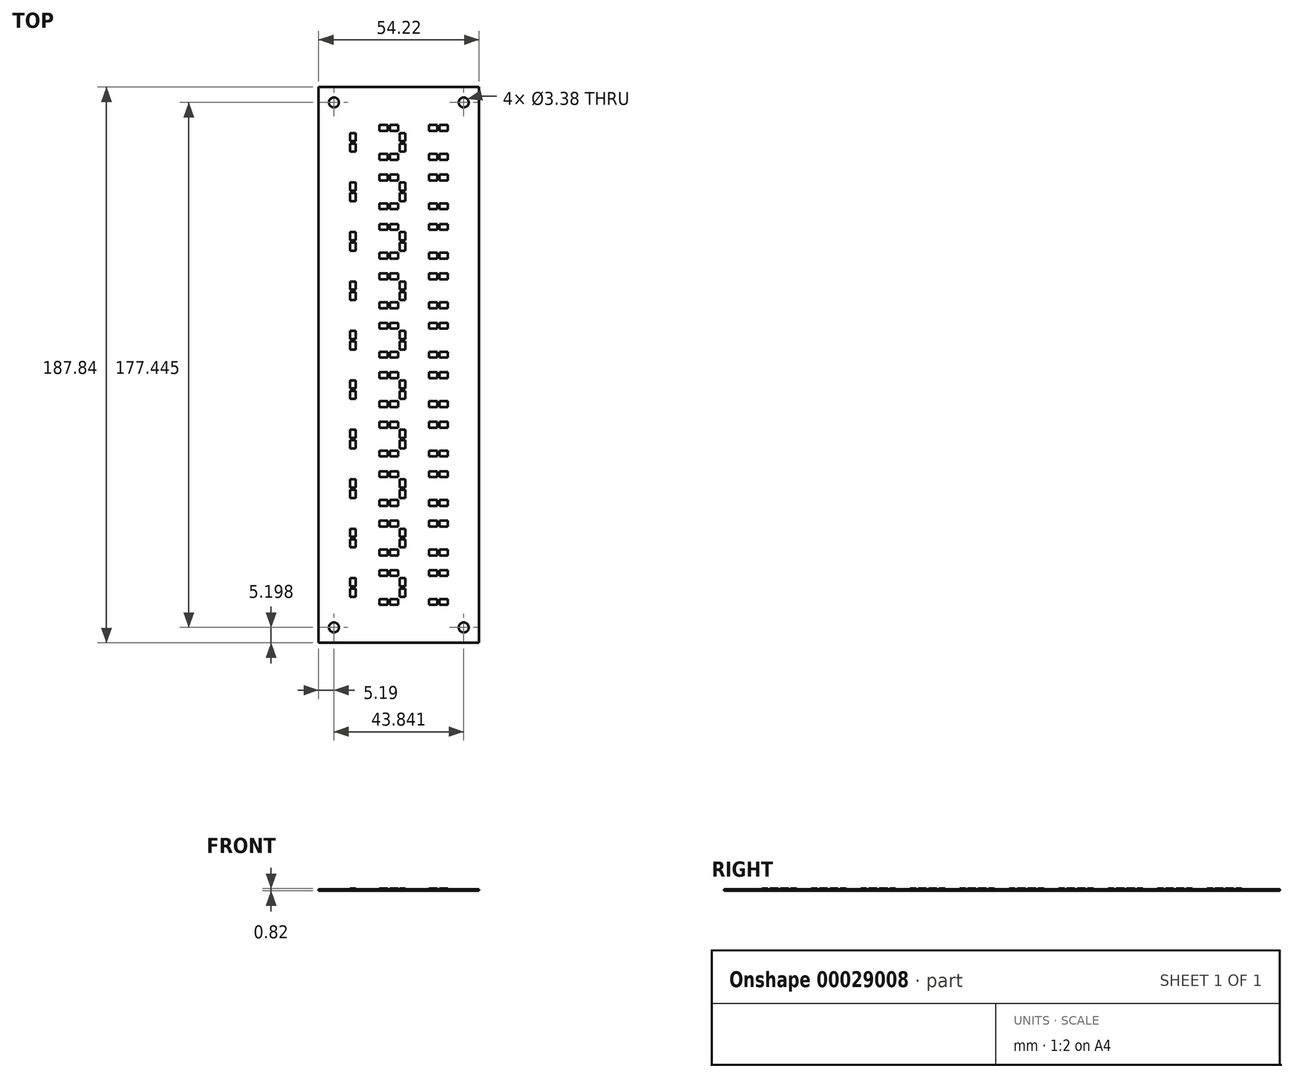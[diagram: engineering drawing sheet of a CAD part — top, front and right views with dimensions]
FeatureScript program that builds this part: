
annotation { "Feature Type Name" : "Feature", "Feature Type Description" : "" }
export const myFeature = defineFeature(function(context is Context, id is Id, definition is map)
    precondition{}
    {
        {
            var Q0;
            Q0=qCreatedBy(makeId("Top.planeOp"),FACE);
            var sketch = newSketch(context, id + "F0", { "sketchPlane" : qUnion([Q0])});
            skLineSegment(sketch, "E0.rect.bottom", {"start": v(-27.11, 93.92) * mm, "end": v(27.11, 93.92) * mm});
            skLineSegment(sketch, "E0.rect.top", {"start": v(-27.11, -93.92) * mm, "end": v(27.11, -93.92) * mm});
            skLineSegment(sketch, "E0.rect.left", {"start": v(-27.11, 93.92) * mm, "end": v(-27.11, -93.92) * mm});
            skLineSegment(sketch, "E0.rect.right", {"start": v(27.11, 93.92) * mm, "end": v(27.11, -93.92) * mm});
            skPoint(sketch, "E0.rect.middle", {"position": v(0, 0) * mm});
            skCircle(sketch, "E1", {"center": v(-21.92, 88.72) * mm, "radius": 1.69 * mm});
            skCircle(sketch, "E2", {"center": v(21.92, 88.72) * mm, "radius": 1.69 * mm});
            skCircle(sketch, "E3", {"center": v(21.92, -88.72) * mm, "radius": 1.69 * mm});
            skCircle(sketch, "E4", {"center": v(-21.92, -88.72) * mm, "radius": 1.69 * mm});
            skSolve(sketch);
        }
        {
            var Q0;
            Q0 = qSketchRegion(id + "F0", true);
            extrude(context, id + "F1", {"entities" : qUnion([Q0]), "depth" : .57 * mm});
        }
        {
            var Q0;
            Q0=makeQuery(id+"F1.opExtrude","CAP_FACE",FACE,{"disambiguationData":[OSD([sQuery(id+"F0.wireOp",EDGE,"E0.rect.bottom"),sQuery(id+"F0.wireOp",EDGE,"E0.rect.top"),sQuery(id+"F0.wireOp",EDGE,"E0.rect.left"),sQuery(id+"F0.wireOp",EDGE,"E0.rect.right"),sQuery(id+"F0.wireOp",EDGE,"E1"),sQuery(id+"F0.wireOp",EDGE,"E2"),sQuery(id+"F0.wireOp",EDGE,"E3"),sQuery(id+"F0.wireOp",EDGE,"E4")])],"isStart":false});
            var sketch = newSketch(context, id + "F2", { "sketchPlane" : qUnion([Q0])});
            skLineSegment(sketch, "E5.bottom", {"start": v(-16.54, -78.36) * mm, "end": v(-14.55, -78.36) * mm});
            skLineSegment(sketch, "E5.top", {"start": v(-16.54, -75.62) * mm, "end": v(-14.55, -75.62) * mm});
            skLineSegment(sketch, "E5.left", {"start": v(-16.54, -78.36) * mm, "end": v(-16.54, -75.62) * mm});
            skLineSegment(sketch, "E5.right", {"start": v(-14.55, -78.36) * mm, "end": v(-14.55, -75.62) * mm});
            skLineSegment(sketch, "E6.bottom", {"start": v(-6.53, -79.1) * mm, "end": v(-3.8, -79.1) * mm});
            skLineSegment(sketch, "E6.top", {"start": v(-6.53, -81.08) * mm, "end": v(-3.8, -81.08) * mm});
            skLineSegment(sketch, "E6.left", {"start": v(-6.53, -79.1) * mm, "end": v(-6.53, -81.08) * mm});
            skLineSegment(sketch, "E6.right", {"start": v(-3.8, -79.1) * mm, "end": v(-3.8, -81.08) * mm});
            skLineSegment(sketch, "E7.bottom", {"start": v(-16.54, -74.8) * mm, "end": v(-14.55, -74.8) * mm});
            skLineSegment(sketch, "E7.top", {"start": v(-16.54, -72.06) * mm, "end": v(-14.55, -72.06) * mm});
            skLineSegment(sketch, "E7.left", {"start": v(-16.54, -74.8) * mm, "end": v(-16.54, -72.06) * mm});
            skLineSegment(sketch, "E7.right", {"start": v(-14.55, -74.8) * mm, "end": v(-14.55, -72.06) * mm});
            skLineSegment(sketch, "E8.left", {"start": v(-2.98, -79.1) * mm, "end": v(-2.98, -81.08) * mm});
            skLineSegment(sketch, "E8.top", {"start": v(-2.98, -81.08) * mm, "end": v(-0.24, -81.08) * mm});
            skLineSegment(sketch, "E8.right", {"start": v(-0.24, -79.1) * mm, "end": v(-0.24, -81.08) * mm});
            skLineSegment(sketch, "E8.bottom", {"start": v(-2.98, -79.1) * mm, "end": v(-0.24, -79.1) * mm});
            skLineSegment(sketch, "E9.top", {"start": v(-2.98, -71.32) * mm, "end": v(-0.24, -71.32) * mm});
            skLineSegment(sketch, "E10.right", {"start": v(-3.8, -69.34) * mm, "end": v(-3.8, -71.32) * mm});
            skLineSegment(sketch, "E9.left", {"start": v(-2.98, -69.34) * mm, "end": v(-2.98, -71.32) * mm});
            skLineSegment(sketch, "E10.top", {"start": v(-6.53, -71.32) * mm, "end": v(-3.8, -71.32) * mm});
            skLineSegment(sketch, "E10.bottom", {"start": v(-6.53, -69.34) * mm, "end": v(-3.8, -69.34) * mm});
            skLineSegment(sketch, "E9.bottom", {"start": v(-2.98, -69.34) * mm, "end": v(-0.24, -69.34) * mm});
            skLineSegment(sketch, "E9.right", {"start": v(-0.24, -69.34) * mm, "end": v(-0.24, -71.32) * mm});
            skLineSegment(sketch, "E10.left", {"start": v(-6.53, -69.34) * mm, "end": v(-6.53, -71.32) * mm});
            skLineSegment(sketch, "E11.top", {"start": v(13.79, -71.32) * mm, "end": v(16.53, -71.32) * mm});
            skLineSegment(sketch, "E12.top", {"start": v(13.79, -81.08) * mm, "end": v(16.53, -81.08) * mm});
            skLineSegment(sketch, "E11.right", {"start": v(16.53, -69.34) * mm, "end": v(16.53, -71.32) * mm});
            skLineSegment(sketch, "E11.bottom", {"start": v(13.79, -69.34) * mm, "end": v(16.53, -69.34) * mm});
            skLineSegment(sketch, "E13.right", {"start": v(2.21, -78.36) * mm, "end": v(2.21, -75.62) * mm});
            skLineSegment(sketch, "E13.left", {"start": v(0.23, -78.36) * mm, "end": v(0.23, -75.62) * mm});
            skLineSegment(sketch, "E13.top", {"start": v(0.23, -75.62) * mm, "end": v(2.21, -75.62) * mm});
            skLineSegment(sketch, "E13.bottom", {"start": v(0.23, -78.36) * mm, "end": v(2.21, -78.36) * mm});
            skLineSegment(sketch, "E12.bottom", {"start": v(13.79, -79.1) * mm, "end": v(16.53, -79.1) * mm});
            skLineSegment(sketch, "E12.right", {"start": v(16.53, -79.1) * mm, "end": v(16.53, -81.08) * mm});
            skLineSegment(sketch, "E14.top", {"start": v(0.23, -72.06) * mm, "end": v(2.21, -72.06) * mm});
            skLineSegment(sketch, "E14.bottom", {"start": v(0.23, -74.8) * mm, "end": v(2.21, -74.8) * mm});
            skLineSegment(sketch, "E11.left", {"start": v(13.79, -69.34) * mm, "end": v(13.79, -71.32) * mm});
            skLineSegment(sketch, "E15.bottom", {"start": v(10.23, -69.34) * mm, "end": v(12.98, -69.34) * mm});
            skLineSegment(sketch, "E15.right", {"start": v(12.98, -69.34) * mm, "end": v(12.98, -71.32) * mm});
            skLineSegment(sketch, "E15.top", {"start": v(10.23, -71.32) * mm, "end": v(12.98, -71.32) * mm});
            skLineSegment(sketch, "E15.left", {"start": v(10.23, -69.34) * mm, "end": v(10.23, -71.32) * mm});
            skLineSegment(sketch, "E12.left", {"start": v(13.79, -79.1) * mm, "end": v(13.79, -81.08) * mm});
            skLineSegment(sketch, "E14.right", {"start": v(2.21, -74.8) * mm, "end": v(2.21, -72.06) * mm});
            skLineSegment(sketch, "E16.left", {"start": v(10.23, -79.1) * mm, "end": v(10.23, -81.08) * mm});
            skLineSegment(sketch, "E16.top", {"start": v(10.23, -81.08) * mm, "end": v(12.98, -81.08) * mm});
            skLineSegment(sketch, "E16.bottom", {"start": v(10.23, -79.1) * mm, "end": v(12.98, -79.1) * mm});
            skLineSegment(sketch, "E14.left", {"start": v(0.23, -74.8) * mm, "end": v(0.23, -72.06) * mm});
            skLineSegment(sketch, "E16.right", {"start": v(12.98, -79.1) * mm, "end": v(12.98, -81.08) * mm});
            skLineSegment(sketch, "E17.left", {"start": v(0.23, -61.65) * mm, "end": v(0.23, -58.9) * mm});
            skLineSegment(sketch, "E18.bottom", {"start": v(-16.54, -61.65) * mm, "end": v(-14.55, -61.65) * mm});
            skLineSegment(sketch, "E19.right", {"start": v(-0.24, -62.38) * mm, "end": v(-0.24, -64.36) * mm});
            skLineSegment(sketch, "E18.top", {"start": v(-16.54, -58.9) * mm, "end": v(-14.55, -58.9) * mm});
            skLineSegment(sketch, "E20.top", {"start": v(-2.98, -54.61) * mm, "end": v(-0.24, -54.61) * mm});
            skLineSegment(sketch, "E19.top", {"start": v(-2.98, -64.36) * mm, "end": v(-0.24, -64.36) * mm});
            skLineSegment(sketch, "E17.right", {"start": v(2.21, -61.65) * mm, "end": v(2.21, -58.9) * mm});
            skLineSegment(sketch, "E21.top", {"start": v(13.79, -54.61) * mm, "end": v(16.53, -54.61) * mm});
            skLineSegment(sketch, "E17.top", {"start": v(0.23, -58.9) * mm, "end": v(2.21, -58.9) * mm});
            skLineSegment(sketch, "E22.right", {"start": v(16.53, -62.38) * mm, "end": v(16.53, -64.36) * mm});
            skLineSegment(sketch, "E18.left", {"start": v(-16.54, -61.65) * mm, "end": v(-16.54, -58.9) * mm});
            skLineSegment(sketch, "E18.right", {"start": v(-14.55, -61.65) * mm, "end": v(-14.55, -58.9) * mm});
            skLineSegment(sketch, "E23.bottom", {"start": v(-16.54, -58.09) * mm, "end": v(-14.55, -58.09) * mm});
            skLineSegment(sketch, "E23.top", {"start": v(-16.54, -55.35) * mm, "end": v(-14.55, -55.35) * mm});
            skLineSegment(sketch, "E22.top", {"start": v(13.79, -64.36) * mm, "end": v(16.53, -64.36) * mm});
            skLineSegment(sketch, "E17.bottom", {"start": v(0.23, -61.65) * mm, "end": v(2.21, -61.65) * mm});
            skLineSegment(sketch, "E24.top", {"start": v(0.23, -55.35) * mm, "end": v(2.21, -55.35) * mm});
            skLineSegment(sketch, "E21.right", {"start": v(16.53, -52.63) * mm, "end": v(16.53, -54.61) * mm});
            skLineSegment(sketch, "E24.bottom", {"start": v(0.23, -58.09) * mm, "end": v(2.21, -58.09) * mm});
            skLineSegment(sketch, "E25.top", {"start": v(10.23, -54.61) * mm, "end": v(12.98, -54.61) * mm});
            skLineSegment(sketch, "E21.bottom", {"start": v(13.79, -52.63) * mm, "end": v(16.53, -52.63) * mm});
            skLineSegment(sketch, "E26.left", {"start": v(10.23, -62.38) * mm, "end": v(10.23, -64.36) * mm});
            skLineSegment(sketch, "E21.left", {"start": v(13.79, -52.63) * mm, "end": v(13.79, -54.61) * mm});
            skLineSegment(sketch, "E27.right", {"start": v(-3.8, -52.63) * mm, "end": v(-3.8, -54.61) * mm});
            skLineSegment(sketch, "E19.bottom", {"start": v(-2.98, -62.38) * mm, "end": v(-0.24, -62.38) * mm});
            skLineSegment(sketch, "E27.left", {"start": v(-6.53, -52.63) * mm, "end": v(-6.53, -54.61) * mm});
            skLineSegment(sketch, "E27.bottom", {"start": v(-6.53, -52.63) * mm, "end": v(-3.8, -52.63) * mm});
            skLineSegment(sketch, "E26.bottom", {"start": v(10.23, -62.38) * mm, "end": v(12.98, -62.38) * mm});
            skLineSegment(sketch, "E22.bottom", {"start": v(13.79, -62.38) * mm, "end": v(16.53, -62.38) * mm});
            skLineSegment(sketch, "E26.top", {"start": v(10.23, -64.36) * mm, "end": v(12.98, -64.36) * mm});
            skLineSegment(sketch, "E25.left", {"start": v(10.23, -52.63) * mm, "end": v(10.23, -54.61) * mm});
            skLineSegment(sketch, "E25.bottom", {"start": v(10.23, -52.63) * mm, "end": v(12.98, -52.63) * mm});
            skLineSegment(sketch, "E20.bottom", {"start": v(-2.98, -52.63) * mm, "end": v(-0.24, -52.63) * mm});
            skLineSegment(sketch, "E24.left", {"start": v(0.23, -58.09) * mm, "end": v(0.23, -55.35) * mm});
            skLineSegment(sketch, "E28.bottom", {"start": v(-6.53, -62.38) * mm, "end": v(-3.8, -62.38) * mm});
            skLineSegment(sketch, "E28.top", {"start": v(-6.53, -64.36) * mm, "end": v(-3.8, -64.36) * mm});
            skLineSegment(sketch, "E28.left", {"start": v(-6.53, -62.38) * mm, "end": v(-6.53, -64.36) * mm});
            skLineSegment(sketch, "E28.right", {"start": v(-3.8, -62.38) * mm, "end": v(-3.8, -64.36) * mm});
            skLineSegment(sketch, "E23.left", {"start": v(-16.54, -58.09) * mm, "end": v(-16.54, -55.35) * mm});
            skLineSegment(sketch, "E23.right", {"start": v(-14.55, -58.09) * mm, "end": v(-14.55, -55.35) * mm});
            skLineSegment(sketch, "E22.left", {"start": v(13.79, -62.38) * mm, "end": v(13.79, -64.36) * mm});
            skLineSegment(sketch, "E19.left", {"start": v(-2.98, -62.38) * mm, "end": v(-2.98, -64.36) * mm});
            skLineSegment(sketch, "E25.right", {"start": v(12.98, -52.63) * mm, "end": v(12.98, -54.61) * mm});
            skLineSegment(sketch, "E20.right", {"start": v(-0.24, -52.63) * mm, "end": v(-0.24, -54.61) * mm});
            skLineSegment(sketch, "E26.right", {"start": v(12.98, -62.38) * mm, "end": v(12.98, -64.36) * mm});
            skLineSegment(sketch, "E20.left", {"start": v(-2.98, -52.63) * mm, "end": v(-2.98, -54.61) * mm});
            skLineSegment(sketch, "E24.right", {"start": v(2.21, -58.09) * mm, "end": v(2.21, -55.35) * mm});
            skLineSegment(sketch, "E27.top", {"start": v(-6.53, -54.61) * mm, "end": v(-3.8, -54.61) * mm});
            skLineSegment(sketch, "E29.top", {"start": v(0.23, -25.48) * mm, "end": v(2.21, -25.48) * mm});
            skLineSegment(sketch, "E30.top", {"start": v(13.79, -37.9) * mm, "end": v(16.53, -37.9) * mm});
            skLineSegment(sketch, "E31.top", {"start": v(0.23, -38.63) * mm, "end": v(2.21, -38.63) * mm});
            skLineSegment(sketch, "E32.top", {"start": v(13.79, -47.65) * mm, "end": v(16.53, -47.65) * mm});
            skLineSegment(sketch, "E33.top", {"start": v(-2.98, -47.65) * mm, "end": v(-0.24, -47.65) * mm});
            skLineSegment(sketch, "E34.bottom", {"start": v(0.23, -24.66) * mm, "end": v(2.21, -24.66) * mm});
            skLineSegment(sketch, "E35.left", {"start": v(-16.54, -28.22) * mm, "end": v(-16.54, -25.48) * mm});
            skLineSegment(sketch, "E30.right", {"start": v(16.53, -35.92) * mm, "end": v(16.53, -37.9) * mm});
            skLineSegment(sketch, "E31.bottom", {"start": v(0.23, -41.38) * mm, "end": v(2.21, -41.38) * mm});
            skLineSegment(sketch, "E36.left", {"start": v(-16.54, -44.93) * mm, "end": v(-16.54, -42.19) * mm});
            skLineSegment(sketch, "E36.right", {"start": v(-14.55, -44.93) * mm, "end": v(-14.55, -42.19) * mm});
            skLineSegment(sketch, "E37.top", {"start": v(-2.98, -37.9) * mm, "end": v(-0.24, -37.9) * mm});
            skLineSegment(sketch, "E38.top", {"start": v(13.79, -21.18) * mm, "end": v(16.53, -21.18) * mm});
            skLineSegment(sketch, "E29.left", {"start": v(0.23, -28.22) * mm, "end": v(0.23, -25.48) * mm});
            skLineSegment(sketch, "E34.top", {"start": v(0.23, -21.92) * mm, "end": v(2.21, -21.92) * mm});
            skLineSegment(sketch, "E29.right", {"start": v(2.21, -28.22) * mm, "end": v(2.21, -25.48) * mm});
            skLineSegment(sketch, "E29.bottom", {"start": v(0.23, -28.22) * mm, "end": v(2.21, -28.22) * mm});
            skLineSegment(sketch, "E39.bottom", {"start": v(0.23, -44.93) * mm, "end": v(2.21, -44.93) * mm});
            skLineSegment(sketch, "E40.top", {"start": v(-2.98, -30.94) * mm, "end": v(-0.24, -30.94) * mm});
            skLineSegment(sketch, "E41.top", {"start": v(13.79, -30.94) * mm, "end": v(16.53, -30.94) * mm});
            skLineSegment(sketch, "E39.top", {"start": v(0.23, -42.19) * mm, "end": v(2.21, -42.19) * mm});
            skLineSegment(sketch, "E39.right", {"start": v(2.21, -44.93) * mm, "end": v(2.21, -42.19) * mm});
            skLineSegment(sketch, "E42.top", {"start": v(-2.98, -21.18) * mm, "end": v(-0.24, -21.18) * mm});
            skLineSegment(sketch, "E39.left", {"start": v(0.23, -44.93) * mm, "end": v(0.23, -42.19) * mm});
            skLineSegment(sketch, "E35.right", {"start": v(-14.55, -28.22) * mm, "end": v(-14.55, -25.48) * mm});
            skLineSegment(sketch, "E43.left", {"start": v(10.23, -35.92) * mm, "end": v(10.23, -37.9) * mm});
            skLineSegment(sketch, "E44.top", {"start": v(-6.53, -47.65) * mm, "end": v(-3.8, -47.65) * mm});
            skLineSegment(sketch, "E33.bottom", {"start": v(-2.98, -45.67) * mm, "end": v(-0.24, -45.67) * mm});
            skLineSegment(sketch, "E37.left", {"start": v(-2.98, -35.92) * mm, "end": v(-2.98, -37.9) * mm});
            skLineSegment(sketch, "E45.right", {"start": v(-14.55, -41.38) * mm, "end": v(-14.55, -38.63) * mm});
            skLineSegment(sketch, "E46.right", {"start": v(-3.8, -35.92) * mm, "end": v(-3.8, -37.9) * mm});
            skLineSegment(sketch, "E34.left", {"start": v(0.23, -24.66) * mm, "end": v(0.23, -21.92) * mm});
            skLineSegment(sketch, "E45.left", {"start": v(-16.54, -41.38) * mm, "end": v(-16.54, -38.63) * mm});
            skLineSegment(sketch, "E47.bottom", {"start": v(-6.53, -28.96) * mm, "end": v(-3.8, -28.96) * mm});
            skLineSegment(sketch, "E48.bottom", {"start": v(-6.53, -19.2) * mm, "end": v(-3.8, -19.2) * mm});
            skLineSegment(sketch, "E31.right", {"start": v(2.21, -41.38) * mm, "end": v(2.21, -38.63) * mm});
            skLineSegment(sketch, "E46.top", {"start": v(-6.53, -37.9) * mm, "end": v(-3.8, -37.9) * mm});
            skLineSegment(sketch, "E49.top", {"start": v(10.23, -21.18) * mm, "end": v(12.98, -21.18) * mm});
            skLineSegment(sketch, "E47.top", {"start": v(-6.53, -30.94) * mm, "end": v(-3.8, -30.94) * mm});
            skLineSegment(sketch, "E44.bottom", {"start": v(-6.53, -45.67) * mm, "end": v(-3.8, -45.67) * mm});
            skLineSegment(sketch, "E40.bottom", {"start": v(-2.98, -28.96) * mm, "end": v(-0.24, -28.96) * mm});
            skLineSegment(sketch, "E50.right", {"start": v(-14.55, -24.66) * mm, "end": v(-14.55, -21.92) * mm});
            skLineSegment(sketch, "E32.bottom", {"start": v(13.79, -45.67) * mm, "end": v(16.53, -45.67) * mm});
            skLineSegment(sketch, "E46.left", {"start": v(-6.53, -35.92) * mm, "end": v(-6.53, -37.9) * mm});
            skLineSegment(sketch, "E43.top", {"start": v(10.23, -37.9) * mm, "end": v(12.98, -37.9) * mm});
            skLineSegment(sketch, "E42.bottom", {"start": v(-2.98, -19.2) * mm, "end": v(-0.24, -19.2) * mm});
            skLineSegment(sketch, "E49.bottom", {"start": v(10.23, -19.2) * mm, "end": v(12.98, -19.2) * mm});
            skLineSegment(sketch, "E50.left", {"start": v(-16.54, -24.66) * mm, "end": v(-16.54, -21.92) * mm});
            skLineSegment(sketch, "E48.top", {"start": v(-6.53, -21.18) * mm, "end": v(-3.8, -21.18) * mm});
            skLineSegment(sketch, "E37.right", {"start": v(-0.24, -35.92) * mm, "end": v(-0.24, -37.9) * mm});
            skLineSegment(sketch, "E43.right", {"start": v(12.98, -35.92) * mm, "end": v(12.98, -37.9) * mm});
            skLineSegment(sketch, "E31.left", {"start": v(0.23, -41.38) * mm, "end": v(0.23, -38.63) * mm});
            skLineSegment(sketch, "E34.right", {"start": v(2.21, -24.66) * mm, "end": v(2.21, -21.92) * mm});
            skLineSegment(sketch, "E37.bottom", {"start": v(-2.98, -35.92) * mm, "end": v(-0.24, -35.92) * mm});
            skLineSegment(sketch, "E43.bottom", {"start": v(10.23, -35.92) * mm, "end": v(12.98, -35.92) * mm});
            skLineSegment(sketch, "E51.top", {"start": v(10.23, -47.65) * mm, "end": v(12.98, -47.65) * mm});
            skLineSegment(sketch, "E41.bottom", {"start": v(13.79, -28.96) * mm, "end": v(16.53, -28.96) * mm});
            skLineSegment(sketch, "E51.bottom", {"start": v(10.23, -45.67) * mm, "end": v(12.98, -45.67) * mm});
            skLineSegment(sketch, "E38.bottom", {"start": v(13.79, -19.2) * mm, "end": v(16.53, -19.2) * mm});
            skLineSegment(sketch, "E52.top", {"start": v(10.23, -30.94) * mm, "end": v(12.98, -30.94) * mm});
            skLineSegment(sketch, "E46.bottom", {"start": v(-6.53, -35.92) * mm, "end": v(-3.8, -35.92) * mm});
            skLineSegment(sketch, "E30.left", {"start": v(13.79, -35.92) * mm, "end": v(13.79, -37.9) * mm});
            skLineSegment(sketch, "E30.bottom", {"start": v(13.79, -35.92) * mm, "end": v(16.53, -35.92) * mm});
            skLineSegment(sketch, "E52.bottom", {"start": v(10.23, -28.96) * mm, "end": v(12.98, -28.96) * mm});
            skLineSegment(sketch, "E33.left", {"start": v(-2.98, -45.67) * mm, "end": v(-2.98, -47.65) * mm});
            skLineSegment(sketch, "E41.left", {"start": v(13.79, -28.96) * mm, "end": v(13.79, -30.94) * mm});
            skLineSegment(sketch, "E32.left", {"start": v(13.79, -45.67) * mm, "end": v(13.79, -47.65) * mm});
            skLineSegment(sketch, "E44.left", {"start": v(-6.53, -45.67) * mm, "end": v(-6.53, -47.65) * mm});
            skLineSegment(sketch, "E36.top", {"start": v(-16.54, -42.19) * mm, "end": v(-14.55, -42.19) * mm});
            skLineSegment(sketch, "E45.bottom", {"start": v(-16.54, -41.38) * mm, "end": v(-14.55, -41.38) * mm});
            skLineSegment(sketch, "E32.right", {"start": v(16.53, -45.67) * mm, "end": v(16.53, -47.65) * mm});
            skLineSegment(sketch, "E36.bottom", {"start": v(-16.54, -44.93) * mm, "end": v(-14.55, -44.93) * mm});
            skLineSegment(sketch, "E40.left", {"start": v(-2.98, -28.96) * mm, "end": v(-2.98, -30.94) * mm});
            skLineSegment(sketch, "E35.bottom", {"start": v(-16.54, -28.22) * mm, "end": v(-14.55, -28.22) * mm});
            skLineSegment(sketch, "E44.right", {"start": v(-3.8, -45.67) * mm, "end": v(-3.8, -47.65) * mm});
            skLineSegment(sketch, "E48.left", {"start": v(-6.53, -19.2) * mm, "end": v(-6.53, -21.18) * mm});
            skLineSegment(sketch, "E33.right", {"start": v(-0.24, -45.67) * mm, "end": v(-0.24, -47.65) * mm});
            skLineSegment(sketch, "E41.right", {"start": v(16.53, -28.96) * mm, "end": v(16.53, -30.94) * mm});
            skLineSegment(sketch, "E38.right", {"start": v(16.53, -19.2) * mm, "end": v(16.53, -21.18) * mm});
            skLineSegment(sketch, "E45.top", {"start": v(-16.54, -38.63) * mm, "end": v(-14.55, -38.63) * mm});
            skLineSegment(sketch, "E40.right", {"start": v(-0.24, -28.96) * mm, "end": v(-0.24, -30.94) * mm});
            skLineSegment(sketch, "E49.right", {"start": v(12.98, -19.2) * mm, "end": v(12.98, -21.18) * mm});
            skLineSegment(sketch, "E35.top", {"start": v(-16.54, -25.48) * mm, "end": v(-14.55, -25.48) * mm});
            skLineSegment(sketch, "E48.right", {"start": v(-3.8, -19.2) * mm, "end": v(-3.8, -21.18) * mm});
            skLineSegment(sketch, "E51.right", {"start": v(12.98, -45.67) * mm, "end": v(12.98, -47.65) * mm});
            skLineSegment(sketch, "E38.left", {"start": v(13.79, -19.2) * mm, "end": v(13.79, -21.18) * mm});
            skLineSegment(sketch, "E52.left", {"start": v(10.23, -28.96) * mm, "end": v(10.23, -30.94) * mm});
            skLineSegment(sketch, "E47.right", {"start": v(-3.8, -28.96) * mm, "end": v(-3.8, -30.94) * mm});
            skLineSegment(sketch, "E49.left", {"start": v(10.23, -19.2) * mm, "end": v(10.23, -21.18) * mm});
            skLineSegment(sketch, "E52.right", {"start": v(12.98, -28.96) * mm, "end": v(12.98, -30.94) * mm});
            skLineSegment(sketch, "E50.bottom", {"start": v(-16.54, -24.66) * mm, "end": v(-14.55, -24.66) * mm});
            skLineSegment(sketch, "E50.top", {"start": v(-16.54, -21.92) * mm, "end": v(-14.55, -21.92) * mm});
            skLineSegment(sketch, "E47.left", {"start": v(-6.53, -28.96) * mm, "end": v(-6.53, -30.94) * mm});
            skLineSegment(sketch, "E42.left", {"start": v(-2.98, -19.2) * mm, "end": v(-2.98, -21.18) * mm});
            skLineSegment(sketch, "E42.right", {"start": v(-0.24, -19.2) * mm, "end": v(-0.24, -21.18) * mm});
            skLineSegment(sketch, "E51.left", {"start": v(10.23, -45.67) * mm, "end": v(10.23, -47.65) * mm});
            skLineSegment(sketch, "E53.left", {"start": v(0.23, 38.63) * mm, "end": v(0.23, 41.38) * mm});
            skLineSegment(sketch, "E54.bottom", {"start": v(0.23, 21.92) * mm, "end": v(2.21, 21.92) * mm});
            skLineSegment(sketch, "E55.right", {"start": v(-14.55, 25.48) * mm, "end": v(-14.55, 28.22) * mm});
            skLineSegment(sketch, "E56.right", {"start": v(-0.24, 21.18) * mm, "end": v(-0.24, 19.2) * mm});
            skLineSegment(sketch, "E57.left", {"start": v(0.23, -11.5) * mm, "end": v(0.23, -8.76) * mm});
            skLineSegment(sketch, "E58.left", {"start": v(10.23, -12.24) * mm, "end": v(10.23, -14.22) * mm});
            skLineSegment(sketch, "E59.right", {"start": v(-14.55, 5.2) * mm, "end": v(-14.55, 7.95) * mm});
            skLineSegment(sketch, "E60.right", {"start": v(-0.24, 37.9) * mm, "end": v(-0.24, 35.91) * mm});
            skLineSegment(sketch, "E53.bottom", {"start": v(0.23, 38.63) * mm, "end": v(2.21, 38.63) * mm});
            skLineSegment(sketch, "E55.left", {"start": v(-16.54, 25.48) * mm, "end": v(-16.54, 28.22) * mm});
            skLineSegment(sketch, "E57.right", {"start": v(2.21, -11.5) * mm, "end": v(2.21, -8.76) * mm});
            skLineSegment(sketch, "E58.top", {"start": v(10.23, -14.22) * mm, "end": v(12.98, -14.22) * mm});
            skLineSegment(sketch, "E61.right", {"start": v(16.53, -12.24) * mm, "end": v(16.53, -14.22) * mm});
            skLineSegment(sketch, "E62.right", {"start": v(-0.24, 4.47) * mm, "end": v(-0.24, 2.49) * mm});
            skLineSegment(sketch, "E60.top", {"start": v(-2.98, 35.91) * mm, "end": v(-0.24, 35.91) * mm});
            skLineSegment(sketch, "E57.bottom", {"start": v(0.23, -11.5) * mm, "end": v(2.21, -11.5) * mm});
            skLineSegment(sketch, "E63.bottom", {"start": v(0.23, 5.2) * mm, "end": v(2.21, 5.2) * mm});
            skLineSegment(sketch, "E58.right", {"start": v(12.98, -12.24) * mm, "end": v(12.98, -14.22) * mm});
            skLineSegment(sketch, "E53.right", {"start": v(2.21, 38.63) * mm, "end": v(2.21, 41.38) * mm});
            skLineSegment(sketch, "E53.top", {"start": v(0.23, 41.38) * mm, "end": v(2.21, 41.38) * mm});
            skLineSegment(sketch, "E56.top", {"start": v(-2.98, 19.2) * mm, "end": v(-0.24, 19.2) * mm});
            skLineSegment(sketch, "E64.right", {"start": v(2.21, 42.19) * mm, "end": v(2.21, 44.93) * mm});
            skLineSegment(sketch, "E64.bottom", {"start": v(0.23, 42.19) * mm, "end": v(2.21, 42.19) * mm});
            skLineSegment(sketch, "E62.top", {"start": v(-2.98, 2.49) * mm, "end": v(-0.24, 2.49) * mm});
            skLineSegment(sketch, "E54.right", {"start": v(2.21, 21.92) * mm, "end": v(2.21, 24.66) * mm});
            skLineSegment(sketch, "E65.left", {"start": v(-16.54, 38.63) * mm, "end": v(-16.54, 41.38) * mm});
            skLineSegment(sketch, "E66.left", {"start": v(-16.54, 8.76) * mm, "end": v(-16.54, 11.5) * mm});
            skLineSegment(sketch, "E63.right", {"start": v(2.21, 5.2) * mm, "end": v(2.21, 7.95) * mm});
            skLineSegment(sketch, "E66.right", {"start": v(-14.55, 8.76) * mm, "end": v(-14.55, 11.5) * mm});
            skLineSegment(sketch, "E65.right", {"start": v(-14.55, 38.63) * mm, "end": v(-14.55, 41.38) * mm});
            skLineSegment(sketch, "E67.top", {"start": v(-2.98, -14.22) * mm, "end": v(-0.24, -14.22) * mm});
            skLineSegment(sketch, "E67.right", {"start": v(-0.24, -12.24) * mm, "end": v(-0.24, -14.22) * mm});
            skLineSegment(sketch, "E68.left", {"start": v(-16.54, -11.5) * mm, "end": v(-16.54, -8.76) * mm});
            skLineSegment(sketch, "E68.right", {"start": v(-14.55, -11.5) * mm, "end": v(-14.55, -8.76) * mm});
            skLineSegment(sketch, "E69.top", {"start": v(-6.53, -14.22) * mm, "end": v(-3.8, -14.22) * mm});
            skLineSegment(sketch, "E69.left", {"start": v(-6.53, -12.24) * mm, "end": v(-6.53, -14.22) * mm});
            skLineSegment(sketch, "E69.right", {"start": v(-3.8, -12.24) * mm, "end": v(-3.8, -14.22) * mm});
            skLineSegment(sketch, "E61.left", {"start": v(13.79, -12.24) * mm, "end": v(13.79, -14.22) * mm});
            skLineSegment(sketch, "E61.top", {"start": v(13.79, -14.22) * mm, "end": v(16.53, -14.22) * mm});
            skLineSegment(sketch, "E67.left", {"start": v(-2.98, -12.24) * mm, "end": v(-2.98, -14.22) * mm});
            skLineSegment(sketch, "E70.right", {"start": v(-14.55, 21.92) * mm, "end": v(-14.55, 24.66) * mm});
            skLineSegment(sketch, "E71.bottom", {"start": v(13.79, 4.47) * mm, "end": v(16.53, 4.47) * mm});
            skLineSegment(sketch, "E72.bottom", {"start": v(10.23, 47.65) * mm, "end": v(12.98, 47.65) * mm});
            skLineSegment(sketch, "E73.bottom", {"start": v(13.79, 30.94) * mm, "end": v(16.53, 30.94) * mm});
            skLineSegment(sketch, "E72.right", {"start": v(12.98, 47.65) * mm, "end": v(12.98, 45.67) * mm});
            skLineSegment(sketch, "E74.right", {"start": v(-0.24, 30.94) * mm, "end": v(-0.24, 28.95) * mm});
            skLineSegment(sketch, "E75.bottom", {"start": v(-6.53, 30.94) * mm, "end": v(-3.8, 30.94) * mm});
            skLineSegment(sketch, "E76.left", {"start": v(0.23, -7.95) * mm, "end": v(0.23, -5.2) * mm});
            skLineSegment(sketch, "E77.left", {"start": v(13.79, 37.9) * mm, "end": v(13.79, 35.91) * mm});
            skLineSegment(sketch, "E77.right", {"start": v(16.53, 37.9) * mm, "end": v(16.53, 35.91) * mm});
            skLineSegment(sketch, "E78.right", {"start": v(2.21, 8.76) * mm, "end": v(2.21, 11.5) * mm});
            skLineSegment(sketch, "E57.top", {"start": v(0.23, -8.76) * mm, "end": v(2.21, -8.76) * mm});
            skLineSegment(sketch, "E66.bottom", {"start": v(-16.54, 8.76) * mm, "end": v(-14.55, 8.76) * mm});
            skLineSegment(sketch, "E71.top", {"start": v(13.79, 2.49) * mm, "end": v(16.53, 2.49) * mm});
            skLineSegment(sketch, "E79.left", {"start": v(10.23, 14.22) * mm, "end": v(10.23, 12.24) * mm});
            skLineSegment(sketch, "E80.bottom", {"start": v(-2.98, 47.65) * mm, "end": v(-0.24, 47.65) * mm});
            skLineSegment(sketch, "E73.left", {"start": v(13.79, 30.94) * mm, "end": v(13.79, 28.95) * mm});
            skLineSegment(sketch, "E58.bottom", {"start": v(10.23, -12.24) * mm, "end": v(12.98, -12.24) * mm});
            skLineSegment(sketch, "E66.top", {"start": v(-16.54, 11.5) * mm, "end": v(-14.55, 11.5) * mm});
            skLineSegment(sketch, "E81.top", {"start": v(10.23, 2.49) * mm, "end": v(12.98, 2.49) * mm});
            skLineSegment(sketch, "E82.top", {"start": v(-2.98, -4.47) * mm, "end": v(-0.24, -4.47) * mm});
            skLineSegment(sketch, "E61.bottom", {"start": v(13.79, -12.24) * mm, "end": v(16.53, -12.24) * mm});
            skLineSegment(sketch, "E81.right", {"start": v(12.98, 4.47) * mm, "end": v(12.98, 2.49) * mm});
            skLineSegment(sketch, "E83.top", {"start": v(13.79, 45.67) * mm, "end": v(16.53, 45.67) * mm});
            skLineSegment(sketch, "E74.left", {"start": v(-2.98, 30.94) * mm, "end": v(-2.98, 28.95) * mm});
            skLineSegment(sketch, "E84.top", {"start": v(10.23, 28.95) * mm, "end": v(12.98, 28.95) * mm});
            skLineSegment(sketch, "E85.top", {"start": v(10.23, 35.91) * mm, "end": v(12.98, 35.91) * mm});
            skLineSegment(sketch, "E86.left", {"start": v(-6.53, 47.65) * mm, "end": v(-6.53, 45.67) * mm});
            skLineSegment(sketch, "E87.top", {"start": v(-16.54, 44.93) * mm, "end": v(-14.55, 44.93) * mm});
            skLineSegment(sketch, "E88.right", {"start": v(-0.24, 14.22) * mm, "end": v(-0.24, 12.24) * mm});
            skLineSegment(sketch, "E74.top", {"start": v(-2.98, 28.95) * mm, "end": v(-0.24, 28.95) * mm});
            skLineSegment(sketch, "E56.bottom", {"start": v(-2.98, 21.18) * mm, "end": v(-0.24, 21.18) * mm});
            skLineSegment(sketch, "E75.left", {"start": v(-6.53, 30.94) * mm, "end": v(-6.53, 28.95) * mm});
            skLineSegment(sketch, "E89.bottom", {"start": v(13.79, -2.5) * mm, "end": v(16.53, -2.5) * mm});
            skLineSegment(sketch, "E81.bottom", {"start": v(10.23, 4.47) * mm, "end": v(12.98, 4.47) * mm});
            skLineSegment(sketch, "E75.right", {"start": v(-3.8, 30.94) * mm, "end": v(-3.8, 28.95) * mm});
            skLineSegment(sketch, "E64.top", {"start": v(0.23, 44.93) * mm, "end": v(2.21, 44.93) * mm});
            skLineSegment(sketch, "E73.top", {"start": v(13.79, 28.95) * mm, "end": v(16.53, 28.95) * mm});
            skLineSegment(sketch, "E78.left", {"start": v(0.23, 8.76) * mm, "end": v(0.23, 11.5) * mm});
            skLineSegment(sketch, "E90.right", {"start": v(16.53, 14.22) * mm, "end": v(16.53, 12.24) * mm});
            skLineSegment(sketch, "E83.right", {"start": v(16.53, 47.65) * mm, "end": v(16.53, 45.67) * mm});
            skLineSegment(sketch, "E59.bottom", {"start": v(-16.54, 5.2) * mm, "end": v(-14.55, 5.2) * mm});
            skLineSegment(sketch, "E65.top", {"start": v(-16.54, 41.38) * mm, "end": v(-14.55, 41.38) * mm});
            skLineSegment(sketch, "E76.top", {"start": v(0.23, -5.2) * mm, "end": v(2.21, -5.2) * mm});
            skLineSegment(sketch, "E82.left", {"start": v(-2.98, -2.5) * mm, "end": v(-2.98, -4.47) * mm});
            skLineSegment(sketch, "E91.top", {"start": v(0.23, 28.22) * mm, "end": v(2.21, 28.22) * mm});
            skLineSegment(sketch, "E92.bottom", {"start": v(-6.53, 4.47) * mm, "end": v(-3.8, 4.47) * mm});
            skLineSegment(sketch, "E78.bottom", {"start": v(0.23, 8.76) * mm, "end": v(2.21, 8.76) * mm});
            skLineSegment(sketch, "E93.left", {"start": v(13.79, 21.18) * mm, "end": v(13.79, 19.2) * mm});
            skLineSegment(sketch, "E84.right", {"start": v(12.98, 30.94) * mm, "end": v(12.98, 28.95) * mm});
            skLineSegment(sketch, "E86.bottom", {"start": v(-6.53, 47.65) * mm, "end": v(-3.8, 47.65) * mm});
            skLineSegment(sketch, "E94.top", {"start": v(-6.53, 12.24) * mm, "end": v(-3.8, 12.24) * mm});
            skLineSegment(sketch, "E79.bottom", {"start": v(10.23, 14.22) * mm, "end": v(12.98, 14.22) * mm});
            skLineSegment(sketch, "E85.bottom", {"start": v(10.23, 37.9) * mm, "end": v(12.98, 37.9) * mm});
            skLineSegment(sketch, "E87.left", {"start": v(-16.54, 42.19) * mm, "end": v(-16.54, 44.93) * mm});
            skLineSegment(sketch, "E64.left", {"start": v(0.23, 42.19) * mm, "end": v(0.23, 44.93) * mm});
            skLineSegment(sketch, "E95.left", {"start": v(10.23, 21.18) * mm, "end": v(10.23, 19.2) * mm});
            skLineSegment(sketch, "E76.bottom", {"start": v(0.23, -7.95) * mm, "end": v(2.21, -7.95) * mm});
            skLineSegment(sketch, "E55.top", {"start": v(-16.54, 28.22) * mm, "end": v(-14.55, 28.22) * mm});
            skLineSegment(sketch, "E96.top", {"start": v(-6.53, -4.47) * mm, "end": v(-3.8, -4.47) * mm});
            skLineSegment(sketch, "E93.top", {"start": v(13.79, 19.2) * mm, "end": v(16.53, 19.2) * mm});
            skLineSegment(sketch, "E79.top", {"start": v(10.23, 12.24) * mm, "end": v(12.98, 12.24) * mm});
            skLineSegment(sketch, "E59.top", {"start": v(-16.54, 7.95) * mm, "end": v(-14.55, 7.95) * mm});
            skLineSegment(sketch, "E91.left", {"start": v(0.23, 25.48) * mm, "end": v(0.23, 28.22) * mm});
            skLineSegment(sketch, "E91.right", {"start": v(2.21, 25.48) * mm, "end": v(2.21, 28.22) * mm});
            skLineSegment(sketch, "E88.bottom", {"start": v(-2.98, 14.22) * mm, "end": v(-0.24, 14.22) * mm});
            skLineSegment(sketch, "E77.top", {"start": v(13.79, 35.91) * mm, "end": v(16.53, 35.91) * mm});
            skLineSegment(sketch, "E78.top", {"start": v(0.23, 11.5) * mm, "end": v(2.21, 11.5) * mm});
            skLineSegment(sketch, "E63.left", {"start": v(0.23, 5.2) * mm, "end": v(0.23, 7.95) * mm});
            skLineSegment(sketch, "E56.left", {"start": v(-2.98, 21.18) * mm, "end": v(-2.98, 19.2) * mm});
            skLineSegment(sketch, "E86.top", {"start": v(-6.53, 45.67) * mm, "end": v(-3.8, 45.67) * mm});
            skLineSegment(sketch, "E89.left", {"start": v(13.79, -2.5) * mm, "end": v(13.79, -4.47) * mm});
            skLineSegment(sketch, "E96.bottom", {"start": v(-6.53, -2.5) * mm, "end": v(-3.8, -2.5) * mm});
            skLineSegment(sketch, "E92.left", {"start": v(-6.53, 4.47) * mm, "end": v(-6.53, 2.49) * mm});
            skLineSegment(sketch, "E90.bottom", {"start": v(13.79, 14.22) * mm, "end": v(16.53, 14.22) * mm});
            skLineSegment(sketch, "E70.top", {"start": v(-16.54, 24.66) * mm, "end": v(-14.55, 24.66) * mm});
            skLineSegment(sketch, "E75.top", {"start": v(-6.53, 28.95) * mm, "end": v(-3.8, 28.95) * mm});
            skLineSegment(sketch, "E54.top", {"start": v(0.23, 24.66) * mm, "end": v(2.21, 24.66) * mm});
            skLineSegment(sketch, "E95.right", {"start": v(12.98, 21.18) * mm, "end": v(12.98, 19.2) * mm});
            skLineSegment(sketch, "E97.bottom", {"start": v(10.23, -2.5) * mm, "end": v(12.98, -2.5) * mm});
            skLineSegment(sketch, "E82.bottom", {"start": v(-2.98, -2.5) * mm, "end": v(-0.24, -2.5) * mm});
            skLineSegment(sketch, "E92.right", {"start": v(-3.8, 4.47) * mm, "end": v(-3.8, 2.49) * mm});
            skLineSegment(sketch, "E81.left", {"start": v(10.23, 4.47) * mm, "end": v(10.23, 2.49) * mm});
            skLineSegment(sketch, "E55.bottom", {"start": v(-16.54, 25.48) * mm, "end": v(-14.55, 25.48) * mm});
            skLineSegment(sketch, "E74.bottom", {"start": v(-2.98, 30.94) * mm, "end": v(-0.24, 30.94) * mm});
            skLineSegment(sketch, "E72.top", {"start": v(10.23, 45.67) * mm, "end": v(12.98, 45.67) * mm});
            skLineSegment(sketch, "E83.left", {"start": v(13.79, 47.65) * mm, "end": v(13.79, 45.67) * mm});
            skLineSegment(sketch, "E97.right", {"start": v(12.98, -2.5) * mm, "end": v(12.98, -4.47) * mm});
            skLineSegment(sketch, "E82.right", {"start": v(-0.24, -2.5) * mm, "end": v(-0.24, -4.47) * mm});
            skLineSegment(sketch, "E90.left", {"start": v(13.79, 14.22) * mm, "end": v(13.79, 12.24) * mm});
            skLineSegment(sketch, "E93.right", {"start": v(16.53, 21.18) * mm, "end": v(16.53, 19.2) * mm});
            skLineSegment(sketch, "E84.bottom", {"start": v(10.23, 30.94) * mm, "end": v(12.98, 30.94) * mm});
            skLineSegment(sketch, "E85.left", {"start": v(10.23, 37.9) * mm, "end": v(10.23, 35.91) * mm});
            skLineSegment(sketch, "E94.right", {"start": v(-3.8, 14.22) * mm, "end": v(-3.8, 12.24) * mm});
            skLineSegment(sketch, "E90.top", {"start": v(13.79, 12.24) * mm, "end": v(16.53, 12.24) * mm});
            skLineSegment(sketch, "E97.top", {"start": v(10.23, -4.47) * mm, "end": v(12.98, -4.47) * mm});
            skLineSegment(sketch, "E96.left", {"start": v(-6.53, -2.5) * mm, "end": v(-6.53, -4.47) * mm});
            skLineSegment(sketch, "E98.bottom", {"start": v(-6.53, 21.18) * mm, "end": v(-3.8, 21.18) * mm});
            skLineSegment(sketch, "E54.left", {"start": v(0.23, 21.92) * mm, "end": v(0.23, 24.66) * mm});
            skLineSegment(sketch, "E73.right", {"start": v(16.53, 30.94) * mm, "end": v(16.53, 28.95) * mm});
            skLineSegment(sketch, "E70.bottom", {"start": v(-16.54, 21.92) * mm, "end": v(-14.55, 21.92) * mm});
            skLineSegment(sketch, "E95.top", {"start": v(10.23, 19.2) * mm, "end": v(12.98, 19.2) * mm});
            skLineSegment(sketch, "E62.bottom", {"start": v(-2.98, 4.47) * mm, "end": v(-0.24, 4.47) * mm});
            skLineSegment(sketch, "E63.top", {"start": v(0.23, 7.95) * mm, "end": v(2.21, 7.95) * mm});
            skLineSegment(sketch, "E97.left", {"start": v(10.23, -2.5) * mm, "end": v(10.23, -4.47) * mm});
            skLineSegment(sketch, "E89.top", {"start": v(13.79, -4.47) * mm, "end": v(16.53, -4.47) * mm});
            skLineSegment(sketch, "E60.bottom", {"start": v(-2.98, 37.9) * mm, "end": v(-0.24, 37.9) * mm});
            skLineSegment(sketch, "E91.bottom", {"start": v(0.23, 25.48) * mm, "end": v(2.21, 25.48) * mm});
            skLineSegment(sketch, "E71.left", {"start": v(13.79, 4.47) * mm, "end": v(13.79, 2.49) * mm});
            skLineSegment(sketch, "E67.bottom", {"start": v(-2.98, -12.24) * mm, "end": v(-0.24, -12.24) * mm});
            skLineSegment(sketch, "E72.left", {"start": v(10.23, 47.65) * mm, "end": v(10.23, 45.67) * mm});
            skLineSegment(sketch, "E68.bottom", {"start": v(-16.54, -11.5) * mm, "end": v(-14.55, -11.5) * mm});
            skLineSegment(sketch, "E77.bottom", {"start": v(13.79, 37.9) * mm, "end": v(16.53, 37.9) * mm});
            skLineSegment(sketch, "E68.top", {"start": v(-16.54, -8.76) * mm, "end": v(-14.55, -8.76) * mm});
            skLineSegment(sketch, "E69.bottom", {"start": v(-6.53, -12.24) * mm, "end": v(-3.8, -12.24) * mm});
            skLineSegment(sketch, "E99.bottom", {"start": v(-16.54, -7.95) * mm, "end": v(-14.55, -7.95) * mm});
            skLineSegment(sketch, "E99.top", {"start": v(-16.54, -5.2) * mm, "end": v(-14.55, -5.2) * mm});
            skLineSegment(sketch, "E99.left", {"start": v(-16.54, -7.95) * mm, "end": v(-16.54, -5.2) * mm});
            skLineSegment(sketch, "E99.right", {"start": v(-14.55, -7.95) * mm, "end": v(-14.55, -5.2) * mm});
            skLineSegment(sketch, "E94.left", {"start": v(-6.53, 14.22) * mm, "end": v(-6.53, 12.24) * mm});
            skLineSegment(sketch, "E71.right", {"start": v(16.53, 4.47) * mm, "end": v(16.53, 2.49) * mm});
            skLineSegment(sketch, "E87.right", {"start": v(-14.55, 42.19) * mm, "end": v(-14.55, 44.93) * mm});
            skLineSegment(sketch, "E84.left", {"start": v(10.23, 30.94) * mm, "end": v(10.23, 28.95) * mm});
            skLineSegment(sketch, "E70.left", {"start": v(-16.54, 21.92) * mm, "end": v(-16.54, 24.66) * mm});
            skLineSegment(sketch, "E62.left", {"start": v(-2.98, 4.47) * mm, "end": v(-2.98, 2.49) * mm});
            skLineSegment(sketch, "E85.right", {"start": v(12.98, 37.9) * mm, "end": v(12.98, 35.91) * mm});
            skLineSegment(sketch, "E65.bottom", {"start": v(-16.54, 38.63) * mm, "end": v(-14.55, 38.63) * mm});
            skLineSegment(sketch, "E95.bottom", {"start": v(10.23, 21.18) * mm, "end": v(12.98, 21.18) * mm});
            skLineSegment(sketch, "E94.bottom", {"start": v(-6.53, 14.22) * mm, "end": v(-3.8, 14.22) * mm});
            skLineSegment(sketch, "E59.left", {"start": v(-16.54, 5.2) * mm, "end": v(-16.54, 7.95) * mm});
            skLineSegment(sketch, "E76.right", {"start": v(2.21, -7.95) * mm, "end": v(2.21, -5.2) * mm});
            skLineSegment(sketch, "E89.right", {"start": v(16.53, -2.5) * mm, "end": v(16.53, -4.47) * mm});
            skLineSegment(sketch, "E93.bottom", {"start": v(13.79, 21.18) * mm, "end": v(16.53, 21.18) * mm});
            skLineSegment(sketch, "E79.right", {"start": v(12.98, 14.22) * mm, "end": v(12.98, 12.24) * mm});
            skLineSegment(sketch, "E87.bottom", {"start": v(-16.54, 42.19) * mm, "end": v(-14.55, 42.19) * mm});
            skLineSegment(sketch, "E98.right", {"start": v(-3.8, 21.18) * mm, "end": v(-3.8, 19.2) * mm});
            skLineSegment(sketch, "E83.bottom", {"start": v(13.79, 47.65) * mm, "end": v(16.53, 47.65) * mm});
            skLineSegment(sketch, "E80.left", {"start": v(-2.98, 47.65) * mm, "end": v(-2.98, 45.67) * mm});
            skLineSegment(sketch, "E100.bottom", {"start": v(-6.53, 37.9) * mm, "end": v(-3.8, 37.9) * mm});
            skLineSegment(sketch, "E88.left", {"start": v(-2.98, 14.22) * mm, "end": v(-2.98, 12.24) * mm});
            skLineSegment(sketch, "E100.left", {"start": v(-6.53, 37.9) * mm, "end": v(-6.53, 35.91) * mm});
            skLineSegment(sketch, "E96.right", {"start": v(-3.8, -2.5) * mm, "end": v(-3.8, -4.47) * mm});
            skLineSegment(sketch, "E80.right", {"start": v(-0.24, 47.65) * mm, "end": v(-0.24, 45.67) * mm});
            skLineSegment(sketch, "E92.top", {"start": v(-6.53, 2.49) * mm, "end": v(-3.8, 2.49) * mm});
            skLineSegment(sketch, "E98.left", {"start": v(-6.53, 21.18) * mm, "end": v(-6.53, 19.2) * mm});
            skLineSegment(sketch, "E86.right", {"start": v(-3.8, 47.65) * mm, "end": v(-3.8, 45.67) * mm});
            skLineSegment(sketch, "E88.top", {"start": v(-2.98, 12.24) * mm, "end": v(-0.24, 12.24) * mm});
            skLineSegment(sketch, "E100.top", {"start": v(-6.53, 35.91) * mm, "end": v(-3.8, 35.91) * mm});
            skLineSegment(sketch, "E80.top", {"start": v(-2.98, 45.67) * mm, "end": v(-0.24, 45.67) * mm});
            skLineSegment(sketch, "E100.right", {"start": v(-3.8, 37.9) * mm, "end": v(-3.8, 35.91) * mm});
            skLineSegment(sketch, "E60.left", {"start": v(-2.98, 37.9) * mm, "end": v(-2.98, 35.91) * mm});
            skLineSegment(sketch, "E98.top", {"start": v(-6.53, 19.2) * mm, "end": v(-3.8, 19.2) * mm});
            skLineSegment(sketch, "E101.top", {"start": v(-2.98, 69.34) * mm, "end": v(-0.24, 69.34) * mm});
            skLineSegment(sketch, "E102.top", {"start": v(0.23, 61.64) * mm, "end": v(2.21, 61.64) * mm});
            skLineSegment(sketch, "E103.top", {"start": v(0.23, 58.09) * mm, "end": v(2.21, 58.09) * mm});
            skLineSegment(sketch, "E104.top", {"start": v(0.23, 74.8) * mm, "end": v(2.21, 74.8) * mm});
            skLineSegment(sketch, "E105.top", {"start": v(-16.54, 58.09) * mm, "end": v(-14.55, 58.09) * mm});
            skLineSegment(sketch, "E102.bottom", {"start": v(0.23, 58.9) * mm, "end": v(2.21, 58.9) * mm});
            skLineSegment(sketch, "E105.left", {"start": v(-16.54, 55.35) * mm, "end": v(-16.54, 58.09) * mm});
            skLineSegment(sketch, "E106.top", {"start": v(-16.54, 78.36) * mm, "end": v(-14.55, 78.36) * mm});
            skLineSegment(sketch, "E107.top", {"start": v(13.79, 52.63) * mm, "end": v(16.53, 52.63) * mm});
            skLineSegment(sketch, "E106.bottom", {"start": v(-16.54, 75.61) * mm, "end": v(-14.55, 75.61) * mm});
            skLineSegment(sketch, "E108.top", {"start": v(-2.98, 52.63) * mm, "end": v(-0.24, 52.63) * mm});
            skLineSegment(sketch, "E109.top", {"start": v(-16.54, 74.8) * mm, "end": v(-14.55, 74.8) * mm});
            skLineSegment(sketch, "E110.top", {"start": v(-16.54, 61.64) * mm, "end": v(-14.55, 61.64) * mm});
            skLineSegment(sketch, "E104.right", {"start": v(2.21, 72.06) * mm, "end": v(2.21, 74.8) * mm});
            skLineSegment(sketch, "E111.right", {"start": v(16.53, 71.32) * mm, "end": v(16.53, 69.34) * mm});
            skLineSegment(sketch, "E103.bottom", {"start": v(0.23, 55.35) * mm, "end": v(2.21, 55.35) * mm});
            skLineSegment(sketch, "E112.right", {"start": v(16.53, 81.07) * mm, "end": v(16.53, 79.1) * mm});
            skLineSegment(sketch, "E113.top", {"start": v(13.79, 62.38) * mm, "end": v(16.53, 62.38) * mm});
            skLineSegment(sketch, "E109.right", {"start": v(-14.55, 72.06) * mm, "end": v(-14.55, 74.8) * mm});
            skLineSegment(sketch, "E104.left", {"start": v(0.23, 72.06) * mm, "end": v(0.23, 74.8) * mm});
            skLineSegment(sketch, "E112.top", {"start": v(13.79, 79.1) * mm, "end": v(16.53, 79.1) * mm});
            skLineSegment(sketch, "E114.bottom", {"start": v(0.23, 75.61) * mm, "end": v(2.21, 75.61) * mm});
            skLineSegment(sketch, "E115.top", {"start": v(-2.98, 62.38) * mm, "end": v(-0.24, 62.38) * mm});
            skLineSegment(sketch, "E109.bottom", {"start": v(-16.54, 72.06) * mm, "end": v(-14.55, 72.06) * mm});
            skLineSegment(sketch, "E101.right", {"start": v(-0.24, 71.32) * mm, "end": v(-0.24, 69.34) * mm});
            skLineSegment(sketch, "E104.bottom", {"start": v(0.23, 72.06) * mm, "end": v(2.21, 72.06) * mm});
            skLineSegment(sketch, "E105.right", {"start": v(-14.55, 55.35) * mm, "end": v(-14.55, 58.09) * mm});
            skLineSegment(sketch, "E103.right", {"start": v(2.21, 55.35) * mm, "end": v(2.21, 58.09) * mm});
            skLineSegment(sketch, "E109.left", {"start": v(-16.54, 72.06) * mm, "end": v(-16.54, 74.8) * mm});
            skLineSegment(sketch, "E103.left", {"start": v(0.23, 55.35) * mm, "end": v(0.23, 58.09) * mm});
            skLineSegment(sketch, "E111.top", {"start": v(13.79, 69.34) * mm, "end": v(16.53, 69.34) * mm});
            skLineSegment(sketch, "E110.bottom", {"start": v(-16.54, 58.9) * mm, "end": v(-14.55, 58.9) * mm});
            skLineSegment(sketch, "E114.top", {"start": v(0.23, 78.36) * mm, "end": v(2.21, 78.36) * mm});
            skLineSegment(sketch, "E105.bottom", {"start": v(-16.54, 55.35) * mm, "end": v(-14.55, 55.35) * mm});
            skLineSegment(sketch, "E116.top", {"start": v(-2.98, 79.1) * mm, "end": v(-0.24, 79.1) * mm});
            skLineSegment(sketch, "E112.left", {"start": v(13.79, 81.07) * mm, "end": v(13.79, 79.1) * mm});
            skLineSegment(sketch, "E117.top", {"start": v(-6.53, 79.1) * mm, "end": v(-3.8, 79.1) * mm});
            skLineSegment(sketch, "E118.bottom", {"start": v(-6.53, 64.36) * mm, "end": v(-3.8, 64.36) * mm});
            skLineSegment(sketch, "E119.left", {"start": v(10.23, 71.32) * mm, "end": v(10.23, 69.34) * mm});
            skLineSegment(sketch, "E114.right", {"start": v(2.21, 75.61) * mm, "end": v(2.21, 78.36) * mm});
            skLineSegment(sketch, "E118.top", {"start": v(-6.53, 62.38) * mm, "end": v(-3.8, 62.38) * mm});
            skLineSegment(sketch, "E101.left", {"start": v(-2.98, 71.32) * mm, "end": v(-2.98, 69.34) * mm});
            skLineSegment(sketch, "E120.left", {"start": v(-6.53, 71.32) * mm, "end": v(-6.53, 69.34) * mm});
            skLineSegment(sketch, "E119.right", {"start": v(12.98, 71.32) * mm, "end": v(12.98, 69.34) * mm});
            skLineSegment(sketch, "E106.left", {"start": v(-16.54, 75.61) * mm, "end": v(-16.54, 78.36) * mm});
            skLineSegment(sketch, "E121.bottom", {"start": v(10.23, 64.36) * mm, "end": v(12.98, 64.36) * mm});
            skLineSegment(sketch, "E117.left", {"start": v(-6.53, 81.07) * mm, "end": v(-6.53, 79.1) * mm});
            skLineSegment(sketch, "E120.bottom", {"start": v(-6.53, 71.32) * mm, "end": v(-3.8, 71.32) * mm});
            skLineSegment(sketch, "E101.bottom", {"start": v(-2.98, 71.32) * mm, "end": v(-0.24, 71.32) * mm});
            skLineSegment(sketch, "E119.top", {"start": v(10.23, 69.34) * mm, "end": v(12.98, 69.34) * mm});
            skLineSegment(sketch, "E110.right", {"start": v(-14.55, 58.9) * mm, "end": v(-14.55, 61.64) * mm});
            skLineSegment(sketch, "E116.left", {"start": v(-2.98, 81.07) * mm, "end": v(-2.98, 79.1) * mm});
            skLineSegment(sketch, "E106.right", {"start": v(-14.55, 75.61) * mm, "end": v(-14.55, 78.36) * mm});
            skLineSegment(sketch, "E121.top", {"start": v(10.23, 62.38) * mm, "end": v(12.98, 62.38) * mm});
            skLineSegment(sketch, "E112.bottom", {"start": v(13.79, 81.07) * mm, "end": v(16.53, 81.07) * mm});
            skLineSegment(sketch, "E111.left", {"start": v(13.79, 71.32) * mm, "end": v(13.79, 69.34) * mm});
            skLineSegment(sketch, "E119.bottom", {"start": v(10.23, 71.32) * mm, "end": v(12.98, 71.32) * mm});
            skLineSegment(sketch, "E122.top", {"start": v(-6.53, 52.63) * mm, "end": v(-3.8, 52.63) * mm});
            skLineSegment(sketch, "E114.left", {"start": v(0.23, 75.61) * mm, "end": v(0.23, 78.36) * mm});
            skLineSegment(sketch, "E120.right", {"start": v(-3.8, 71.32) * mm, "end": v(-3.8, 69.34) * mm});
            skLineSegment(sketch, "E123.top", {"start": v(10.23, 79.1) * mm, "end": v(12.98, 79.1) * mm});
            skLineSegment(sketch, "E124.top", {"start": v(10.23, 52.63) * mm, "end": v(12.98, 52.63) * mm});
            skLineSegment(sketch, "E123.left", {"start": v(10.23, 81.07) * mm, "end": v(10.23, 79.1) * mm});
            skLineSegment(sketch, "E116.right", {"start": v(-0.24, 81.07) * mm, "end": v(-0.24, 79.1) * mm});
            skLineSegment(sketch, "E108.bottom", {"start": v(-2.98, 54.6) * mm, "end": v(-0.24, 54.6) * mm});
            skLineSegment(sketch, "E116.bottom", {"start": v(-2.98, 81.07) * mm, "end": v(-0.24, 81.07) * mm});
            skLineSegment(sketch, "E102.left", {"start": v(0.23, 58.9) * mm, "end": v(0.23, 61.64) * mm});
            skLineSegment(sketch, "E124.bottom", {"start": v(10.23, 54.6) * mm, "end": v(12.98, 54.6) * mm});
            skLineSegment(sketch, "E102.right", {"start": v(2.21, 58.9) * mm, "end": v(2.21, 61.64) * mm});
            skLineSegment(sketch, "E111.bottom", {"start": v(13.79, 71.32) * mm, "end": v(16.53, 71.32) * mm});
            skLineSegment(sketch, "E110.left", {"start": v(-16.54, 58.9) * mm, "end": v(-16.54, 61.64) * mm});
            skLineSegment(sketch, "E122.bottom", {"start": v(-6.53, 54.6) * mm, "end": v(-3.8, 54.6) * mm});
            skLineSegment(sketch, "E117.right", {"start": v(-3.8, 81.07) * mm, "end": v(-3.8, 79.1) * mm});
            skLineSegment(sketch, "E123.bottom", {"start": v(10.23, 81.07) * mm, "end": v(12.98, 81.07) * mm});
            skLineSegment(sketch, "E117.bottom", {"start": v(-6.53, 81.07) * mm, "end": v(-3.8, 81.07) * mm});
            skLineSegment(sketch, "E113.bottom", {"start": v(13.79, 64.36) * mm, "end": v(16.53, 64.36) * mm});
            skLineSegment(sketch, "E120.top", {"start": v(-6.53, 69.34) * mm, "end": v(-3.8, 69.34) * mm});
            skLineSegment(sketch, "E123.right", {"start": v(12.98, 81.07) * mm, "end": v(12.98, 79.1) * mm});
            skLineSegment(sketch, "E115.bottom", {"start": v(-2.98, 64.36) * mm, "end": v(-0.24, 64.36) * mm});
            skLineSegment(sketch, "E107.bottom", {"start": v(13.79, 54.6) * mm, "end": v(16.53, 54.6) * mm});
            skLineSegment(sketch, "E108.right", {"start": v(-0.24, 54.6) * mm, "end": v(-0.24, 52.63) * mm});
            skLineSegment(sketch, "E107.right", {"start": v(16.53, 54.6) * mm, "end": v(16.53, 52.63) * mm});
            skLineSegment(sketch, "E121.left", {"start": v(10.23, 64.36) * mm, "end": v(10.23, 62.38) * mm});
            skLineSegment(sketch, "E115.left", {"start": v(-2.98, 64.36) * mm, "end": v(-2.98, 62.38) * mm});
            skLineSegment(sketch, "E115.right", {"start": v(-0.24, 64.36) * mm, "end": v(-0.24, 62.38) * mm});
            skLineSegment(sketch, "E124.left", {"start": v(10.23, 54.6) * mm, "end": v(10.23, 52.63) * mm});
            skLineSegment(sketch, "E122.right", {"start": v(-3.8, 54.6) * mm, "end": v(-3.8, 52.63) * mm});
            skLineSegment(sketch, "E108.left", {"start": v(-2.98, 54.6) * mm, "end": v(-2.98, 52.63) * mm});
            skLineSegment(sketch, "E124.right", {"start": v(12.98, 54.6) * mm, "end": v(12.98, 52.63) * mm});
            skLineSegment(sketch, "E118.left", {"start": v(-6.53, 64.36) * mm, "end": v(-6.53, 62.38) * mm});
            skLineSegment(sketch, "E113.left", {"start": v(13.79, 64.36) * mm, "end": v(13.79, 62.38) * mm});
            skLineSegment(sketch, "E107.left", {"start": v(13.79, 54.6) * mm, "end": v(13.79, 52.63) * mm});
            skLineSegment(sketch, "E122.left", {"start": v(-6.53, 54.6) * mm, "end": v(-6.53, 52.63) * mm});
            skLineSegment(sketch, "E121.right", {"start": v(12.98, 64.36) * mm, "end": v(12.98, 62.38) * mm});
            skLineSegment(sketch, "E118.right", {"start": v(-3.8, 64.36) * mm, "end": v(-3.8, 62.38) * mm});
            skLineSegment(sketch, "E113.right", {"start": v(16.53, 64.36) * mm, "end": v(16.53, 62.38) * mm});
            skSolve(sketch);
        }
        {
            var Q0;
            Q0 = qSketchRegion(id + "F2", true);
            extrude(context, id + "F3", {"entities" : qUnion([Q0]), "operationType" : NewBodyOperationType.ADD, "depth" : .25 * mm});
        }
    });
